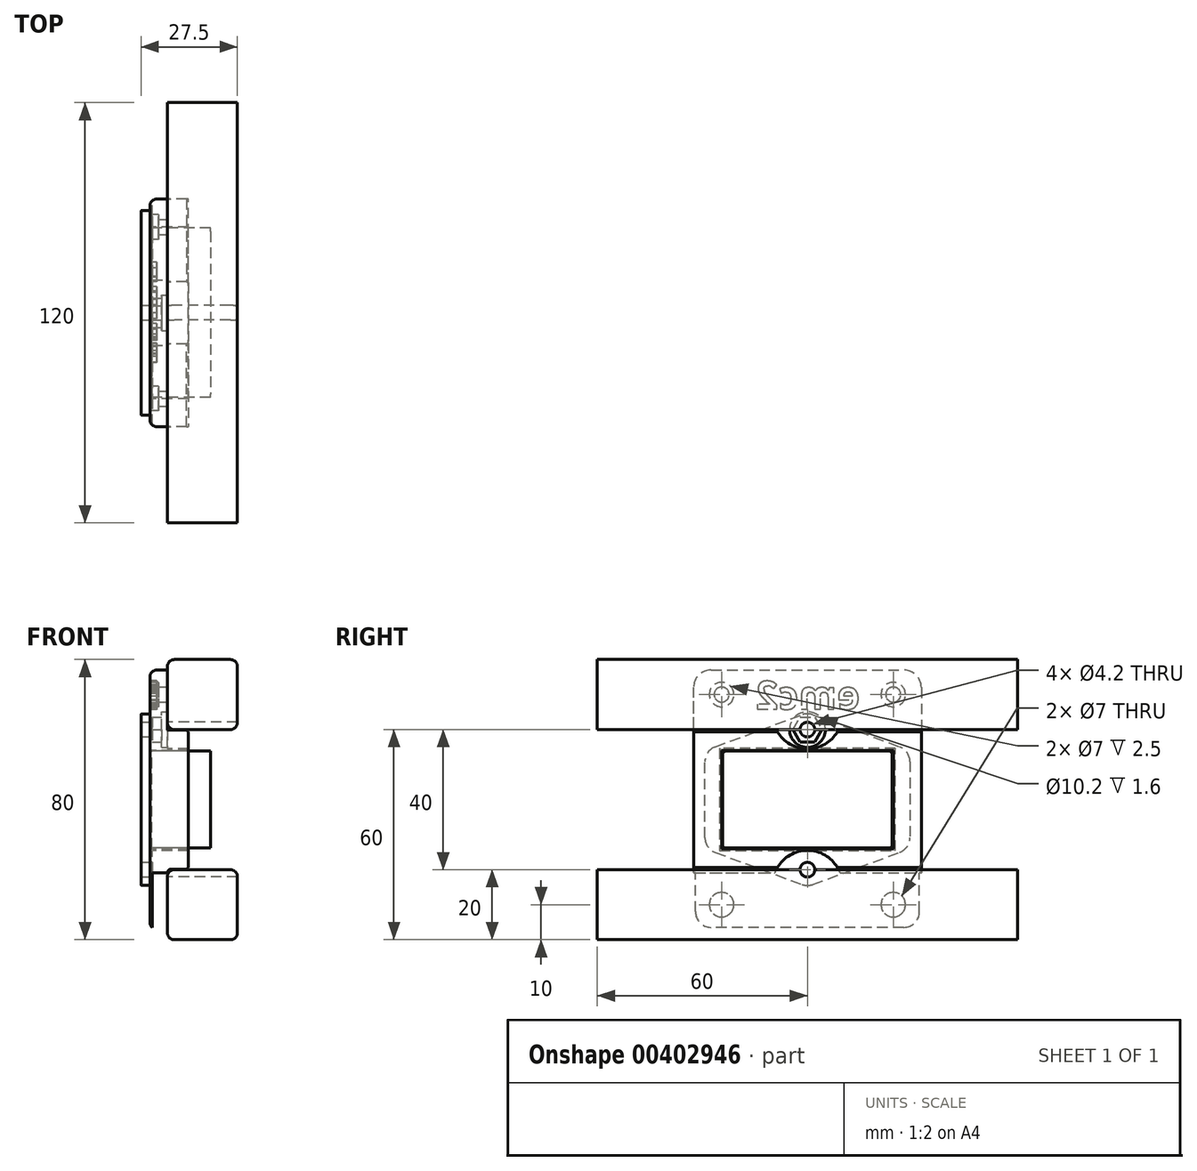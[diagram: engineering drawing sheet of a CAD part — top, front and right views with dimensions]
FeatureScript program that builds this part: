
annotation { "Feature Type Name" : "Feature", "Feature Type Description" : "" }
export const myFeature = defineFeature(function(context is Context, id is Id, definition is map)
    precondition{}
    {
        {
            var Q0;
            Q0=qCreatedBy(makeId("Right.planeOp"),FACE);
            var sketch = newSketch(context, id + "F0", { "sketchPlane" : qUnion([Q0])});
            skLineSegment(sketch, "E0.bottom", {"start": v(-32.5, 19.9) * mm, "end": v(32.5, 19.9) * mm});
            skLineSegment(sketch, "E0.top", {"start": v(-32.5, -19.9) * mm, "end": v(32.5, -19.9) * mm});
            skLineSegment(sketch, "E0.left", {"start": v(-32.5, 19.9) * mm, "end": v(-32.5, -19.9) * mm});
            skLineSegment(sketch, "E0.right", {"start": v(32.5, 19.9) * mm, "end": v(32.5, -19.9) * mm});
            skLineSegment(sketch, "E1.bottom", {"start": v(-24.5, 14) * mm, "end": v(24.5, 14) * mm});
            skLineSegment(sketch, "E1.top", {"start": v(-24.5, -14) * mm, "end": v(24.5, -14) * mm});
            skLineSegment(sketch, "E1.left", {"start": v(-24.5, 14) * mm, "end": v(-24.5, -14) * mm});
            skLineSegment(sketch, "E1.right", {"start": v(24.5, 14) * mm, "end": v(24.5, -14) * mm});
            skLineSegment(sketch, "E2", {"start": v(-32.5, 19.9) * mm, "end": v(-32.5, 37) * mm});
            skLineSegment(sketch, "E3", {"start": v(-32.5, 37) * mm, "end": v(32.5, 37) * mm});
            skLineSegment(sketch, "E4", {"start": v(32.5, 37) * mm, "end": v(32.5, 19.9) * mm});
            skLineSegment(sketch, "E5", {"start": v(-32.5, -19.9) * mm, "end": v(-32.5, -37) * mm});
            skLineSegment(sketch, "E6", {"start": v(-32.5, -37) * mm, "end": v(32.5, -37) * mm});
            skLineSegment(sketch, "E7", {"start": v(32.5, -37) * mm, "end": v(32.5, -19.9) * mm});
            skCircle(sketch, "E8", {"center": v(24.5, 30) * mm, "radius": 2.15 * mm});
            skCircle(sketch, "E9", {"center": v(-24.5, 30) * mm, "radius": 2.15 * mm});
            skCircle(sketch, "E10.MirrorC", {"center": v(-24.5, -30) * mm, "radius": 2.15 * mm});
            skCircle(sketch, "E11.MirrorC", {"center": v(24.5, -30) * mm, "radius": 2.15 * mm});
            skArc(sketch, "E12", {"start": v(-8.88, 19.9) * mm, "mid": v(0, 14.5) * mm, "end": v(8.88, 19.9) * mm});
            skArc(sketch, "E13.MirrorCS", {"start": v(-8.88, -19.9) * mm, "mid": v(0, -14.5) * mm, "end": v(8.88, -19.9) * mm});
            skSolve(sketch);
        }
        {
            var Q0;
            {var subQ1=sQuery(id+"F0.wireOp",EDGE,"E0.left");Q0=makeQuery(id+"F0.imprint","IMPRINT",FACE,{"disambiguationData":[TD([[makeQuery(id+"F0.imprint","IMPRINT",EDGE,{"derivedFrom":subQ1}),1.0]])]});}
            extrude(context, id + "F1", {"entities" : qUnion([Q0]), "depth" : 6 * mm});
        }
        {
            var Q0;
            {var subQ0=sQuery(id+"F0.wireOp",EDGE,"E12");Q0=makeQuery(id+"F0.imprint","IMPRINT",FACE,{"disambiguationData":[TD([[makeQuery(id+"F0.imprint","IMPRINT",EDGE,{"derivedFrom":subQ0}),1.0]])]});}
            var Q1;
            Q1=makeQuery(id+"F0.imprint","IMPRINT",FACE,{"disambiguationData":[TD([[makeQuery(id+"F0.imprint","IMPRINT",EDGE,{"derivedFrom":sQuery(id+"F0.wireOp",EDGE,"E0.top")}),1.0]])]});
            var Q2;
            {var subQ5=sQuery(id+"F0.wireOp",EDGE,"E2");Q2=makeQuery(id+"F0.imprint","IMPRINT",FACE,{"disambiguationData":[TD([[makeQuery(id+"F0.imprint","IMPRINT",EDGE,{"derivedFrom":subQ5}),-1.0]])]});}
            var Q3;
            Q3=makeQuery(id+"F0.imprint","IMPRINT",FACE,{"disambiguationData":[TD([[makeQuery(id+"F0.imprint","IMPRINT",EDGE,{"derivedFrom":sQuery(id+"F0.wireOp",EDGE,"E0.top")}),-1.0]])]});
            var Q4;
            {var subQ1=sQuery(id+"F0.wireOp",EDGE,"E0.left");Q4=makeQuery(id+"F0.imprint","IMPRINT",FACE,{"disambiguationData":[TD([[makeQuery(id+"F0.imprint","IMPRINT",EDGE,{"derivedFrom":subQ1}),1.0]])]});}
            extrude(context, id + "F2", {"entities" : qUnion([Q0, Q1, Q2, Q3, Q4]), "operationType" : NewBodyOperationType.ADD, "oppositeDirection" : true, "depth" : 5 * mm});
        }
        {
            var Q0;
            Q0=qCreatedBy(makeId("Front.planeOp"),FACE);
            var sketch = newSketch(context, id + "F3", { "sketchPlane" : qUnion([Q0])});
            skLineSegment(sketch, "E14.bottom", {"start": v(2, 40) * mm, "end": v(18, 40) * mm});
            skLineSegment(sketch, "E14.top", {"start": v(2, 20) * mm, "end": v(18, 20) * mm});
            skLineSegment(sketch, "E14.left", {"start": v(0, 38) * mm, "end": v(0, 22) * mm});
            skLineSegment(sketch, "E14.right", {"start": v(20, 38) * mm, "end": v(20, 22) * mm});
            skPoint(sketch, "E15.visualSharp", {"position": v(0, 40) * mm});
            skArc(sketch, "E15.filletArc", {"start": v(2, 40) * mm, "mid": v(0.59, 39.41) * mm, "end": v(0, 38) * mm});
            skPoint(sketch, "E16.visualSharp", {"position": v(20, 40) * mm});
            skArc(sketch, "E16.filletArc", {"start": v(20, 38) * mm, "mid": v(19.41, 39.41) * mm, "end": v(18, 40) * mm});
            skPoint(sketch, "E17.visualSharp", {"position": v(20, 20) * mm});
            skArc(sketch, "E17.filletArc", {"start": v(18, 20) * mm, "mid": v(19.41, 20.59) * mm, "end": v(20, 22) * mm});
            skPoint(sketch, "E18.visualSharp", {"position": v(0, 20) * mm});
            skArc(sketch, "E18.filletArc", {"start": v(0, 22) * mm, "mid": v(0.59, 20.59) * mm, "end": v(2, 20) * mm});
            skArc(sketch, "E19.MirrorCS", {"start": v(2, -40) * mm, "mid": v(0.59, -39.41) * mm, "end": v(0, -38) * mm});
            skArc(sketch, "E20.MirrorCS", {"start": v(0, -22) * mm, "mid": v(0.59, -20.59) * mm, "end": v(2, -20) * mm});
            skArc(sketch, "E21.MirrorCS", {"start": v(18, -20) * mm, "mid": v(19.41, -20.59) * mm, "end": v(20, -22) * mm});
            skArc(sketch, "E22.MirrorCS", {"start": v(20, -38) * mm, "mid": v(19.41, -39.41) * mm, "end": v(18, -40) * mm});
            skPoint(sketch, "E23.MirrorP", {"position": v(20, -40) * mm});
            skLineSegment(sketch, "E24.MirrorCS", {"start": v(2, -40) * mm, "end": v(18, -40) * mm});
            skPoint(sketch, "E25.MirrorP", {"position": v(0, -40) * mm});
            skPoint(sketch, "E26.MirrorP", {"position": v(0, -20) * mm});
            skLineSegment(sketch, "E27.MirrorCS", {"start": v(2, -20) * mm, "end": v(18, -20) * mm});
            skPoint(sketch, "E28.MirrorP", {"position": v(20, -20) * mm});
            skLineSegment(sketch, "E29.MirrorCS", {"start": v(0, -38) * mm, "end": v(0, -22) * mm});
            skLineSegment(sketch, "E30.MirrorCS", {"start": v(20, -38) * mm, "end": v(20, -22) * mm});
            skSolve(sketch);
        }
        {
            var Q0;
            Q0 = qSketchRegion(id + "F3", true);
            extrude(context, id + "F4", {"entities" : qUnion([Q0]), "endBound" : BoundingType.SYMMETRIC, "depth" : 120 * mm});
        }
        {
            var Q0;
            Q0=makeQuery(id+"F2.opExtrude","CAP_FACE",FACE,{"disambiguationData":[OSD([sQuery(id+"F0.wireOp",EDGE,"E0.left"),sQuery(id+"F0.wireOp",EDGE,"E0.right"),sQuery(id+"F0.wireOp",EDGE,"E1.bottom"),sQuery(id+"F0.wireOp",EDGE,"E1.top"),sQuery(id+"F0.wireOp",EDGE,"E1.left"),sQuery(id+"F0.wireOp",EDGE,"E1.right"),sQuery(id+"F0.wireOp",EDGE,"E2"),sQuery(id+"F0.wireOp",EDGE,"E3"),sQuery(id+"F0.wireOp",EDGE,"E4"),sQuery(id+"F0.wireOp",EDGE,"E5"),sQuery(id+"F0.wireOp",EDGE,"E6"),sQuery(id+"F0.wireOp",EDGE,"E7"),sQuery(id+"F0.wireOp",EDGE,"E8"),sQuery(id+"F0.wireOp",EDGE,"E9"),sQuery(id+"F0.wireOp",EDGE,"E10.MirrorC"),sQuery(id+"F0.wireOp",EDGE,"E11.MirrorC")])],"isStart":false});
            var sketch = newSketch(context, id + "F5", { "sketchPlane" : qUnion([Q0])});
            skLineSegment(sketch, "E31.bottom", {"start": v(-24.2, 13.85) * mm, "end": v(24.2, 13.85) * mm});
            skLineSegment(sketch, "E31.top", {"start": v(-24.2, -13.85) * mm, "end": v(24.2, -13.85) * mm});
            skLineSegment(sketch, "E31.left", {"start": v(-24.2, 13.85) * mm, "end": v(-24.2, -13.85) * mm});
            skLineSegment(sketch, "E31.right", {"start": v(24.2, 13.85) * mm, "end": v(24.2, -13.85) * mm});
            skLineSegment(sketch, "E32", {"start": v(29.25, 0) * mm, "end": v(29.25, 10.86) * mm});
            skLineSegment(sketch, "E33", {"start": v(26.3, 15.09) * mm, "end": v(1.56, 24.22) * mm});
            skLineSegment(sketch, "E34", {"start": v(-1.56, 24.22) * mm, "end": v(-26.3, 15.09) * mm});
            skLineSegment(sketch, "E35", {"start": v(-29.25, 10.86) * mm, "end": v(-29.25, 0) * mm});
            skPoint(sketch, "E36.visualSharp", {"position": v(0, 24.8) * mm});
            skArc(sketch, "E36.filletArc", {"start": v(1.56, 24.22) * mm, "mid": v(0, 24.5) * mm, "end": v(-1.56, 24.22) * mm});
            skPoint(sketch, "E37.visualSharp", {"position": v(-29.25, 14) * mm});
            skArc(sketch, "E37.filletArc", {"start": v(-26.3, 15.09) * mm, "mid": v(-28.44, 13.44) * mm, "end": v(-29.25, 10.86) * mm});
            skPoint(sketch, "E38.visualSharp", {"position": v(29.25, 14) * mm});
            skArc(sketch, "E38.filletArc", {"start": v(29.25, 10.86) * mm, "mid": v(28.44, 13.44) * mm, "end": v(26.3, 15.09) * mm});
            skLineSegment(sketch, "E39.MirrorCS", {"start": v(-29.25, -10.86) * mm, "end": v(-29.25, 0) * mm});
            skArc(sketch, "E40.MirrorCS", {"start": v(-26.3, -15.09) * mm, "mid": v(-28.44, -13.44) * mm, "end": v(-29.25, -10.86) * mm});
            skLineSegment(sketch, "E41.MirrorCS", {"start": v(-1.56, -24.22) * mm, "end": v(-26.3, -15.09) * mm});
            skLineSegment(sketch, "E42.MirrorCS", {"start": v(26.3, -15.09) * mm, "end": v(1.56, -24.22) * mm});
            skArc(sketch, "E43.MirrorCS", {"start": v(29.25, -10.86) * mm, "mid": v(28.44, -13.44) * mm, "end": v(26.3, -15.09) * mm});
            skLineSegment(sketch, "E44.MirrorCS", {"start": v(29.25, 0) * mm, "end": v(29.25, -10.86) * mm});
            skArc(sketch, "E45.MirrorCS", {"start": v(1.56, -24.22) * mm, "mid": v(0, -24.5) * mm, "end": v(-1.56, -24.22) * mm});
            skCircle(sketch, "E46", {"center": v(0, 20) * mm, "radius": 2.1 * mm});
            skCircle(sketch, "E47.MirrorC", {"center": v(0, -20) * mm, "radius": 2.1 * mm});
            skSolve(sketch);
        }
        {
            var Q0;
            Q0 = qSketchRegion(id + "F5", true);
            var Q1;
            Q1=makeQuery(id+"F5.imprint","IMPRINT",FACE,{"disambiguationData":[TD([[makeQuery(id+"F5.imprint","IMPRINT",EDGE,{"derivedFrom":sQuery(id+"F5.wireOp",EDGE,"E31.bottom")}),-1.0]])]});
            extrude(context, id + "F6", {"entities" : qUnion([Q0, Q1]), "depth" : 2.5 * mm});
        }
        {
            var Q0;
            Q0=makeQuery(id+"F5.imprint","IMPRINT",FACE,{"disambiguationData":[TD([[makeQuery(id+"F5.imprint","IMPRINT",EDGE,{"derivedFrom":sQuery(id+"F5.wireOp",EDGE,"E31.bottom")}),-1.0]])]});
            extrude(context, id + "F7", {"entities" : qUnion([Q0]), "operationType" : NewBodyOperationType.ADD, "oppositeDirection" : true, "depth" : 17.3 * mm});
        }
        {
            var Q0;
            Q0=makeQuery(id+"F7.opExtrude","SWEPT_EDGE",EDGE,{"disambiguationData":[OSD([sQuery(id+"F5.wireOp",EDGE,"E31.bottom"),sQuery(id+"F5.wireOp",EDGE,"E31.right")])]});
            var Q1;
            Q1=makeQuery(id+"F7.opExtrude","SWEPT_EDGE",EDGE,{"disambiguationData":[OSD([sQuery(id+"F5.wireOp",EDGE,"E31.top"),sQuery(id+"F5.wireOp",EDGE,"E31.right")])]});
            var Q2;
            Q2=makeQuery(id+"F7.opExtrude","SWEPT_EDGE",EDGE,{"disambiguationData":[OSD([sQuery(id+"F5.wireOp",EDGE,"E31.top"),sQuery(id+"F5.wireOp",EDGE,"E31.left")])]});
            var Q3;
            Q3=makeQuery(id+"F7.opExtrude","SWEPT_EDGE",EDGE,{"disambiguationData":[OSD([sQuery(id+"F5.wireOp",EDGE,"E31.bottom"),sQuery(id+"F5.wireOp",EDGE,"E31.left")])]});
            fillet(context, id + "F8", {"entities" : qUnion([Q0, Q1, Q2, Q3]), "radius" : 1 * mm, "tangentPropagation" : true, "allowEdgeOverflow" : false});
        }
        {
            var Q0;
            Q0=makeQuery(id+"F6.opExtrude","CAP_EDGE",EDGE,{"disambiguationData":[OSD([sQuery(id+"F5.wireOp",EDGE,"E33")])],"isStart":false});
            fillet(context, id + "F9", {"entities" : qUnion([Q0]), "radius" : 0.2 * mm, "tangentPropagation" : true, "allowEdgeOverflow" : false});
        }
        {
            var Q0;
            Q0=makeQuery(id+"F2.opExtrude","SWEPT_EDGE",EDGE,{"disambiguationData":[OSD([sQuery(id+"F0.wireOp",EDGE,"E2"),sQuery(id+"F0.wireOp",EDGE,"E3")])]});
            var Q1;
            Q1=makeQuery(id+"F2.opExtrude","SWEPT_EDGE",EDGE,{"disambiguationData":[OSD([sQuery(id+"F0.wireOp",EDGE,"E3"),sQuery(id+"F0.wireOp",EDGE,"E4")])]});
            var Q2;
            Q2=makeQuery(id+"F2.opExtrude","SWEPT_EDGE",EDGE,{"disambiguationData":[OSD([sQuery(id+"F0.wireOp",EDGE,"E6"),sQuery(id+"F0.wireOp",EDGE,"E7")])]});
            var Q3;
            Q3=makeQuery(id+"F2.opExtrude","SWEPT_EDGE",EDGE,{"disambiguationData":[OSD([sQuery(id+"F0.wireOp",EDGE,"E5"),sQuery(id+"F0.wireOp",EDGE,"E6")])]});
            fillet(context, id + "F10", {"entities" : qUnion([Q0, Q1, Q2, Q3]), "radius" : 5 * mm, "tangentPropagation" : true, "allowEdgeOverflow" : false});
        }
        {
            var Q0;
            Q0=makeQuery(id+"F2.opExtrude","CAP_EDGE",EDGE,{"disambiguationData":[OSD([sQuery(id+"F0.wireOp",EDGE,"E3")])],"isStart":false});
            var Q1;
            Q1=makeQuery(id+"F2.opExtrude","CAP_EDGE",EDGE,{"disambiguationData":[OSD([sQuery(id+"F0.wireOp",EDGE,"E6")])],"isStart":false});
            fillet(context, id + "F11", {"entities" : qUnion([Q0, Q1]), "radius" : 2 * mm, "tangentPropagation" : true, "allowEdgeOverflow" : false});
        }
        {
            var Q0;
            Q0=makeQuery(id+"F1.opExtrude","CAP_EDGE",EDGE,{"disambiguationData":[OSD([sQuery(id+"F0.wireOp",EDGE,"E0.bottom")])],"isStart":false});
            var Q1;
            Q1=makeQuery(id+"F1.opExtrude","CAP_EDGE",EDGE,{"disambiguationData":[OSD([sQuery(id+"F0.wireOp",EDGE,"E0.top")])],"isStart":false});
            chamfer(context, id + "F12", {"entities" : qUnion([Q0, Q1]), "width" : 0.5 * mm, "tangentPropagation" : true});
        }
        {
            var Q0;
            Q0=makeQuery(id+"F1.opExtrude","CAP_EDGE",EDGE,{"disambiguationData":[OSD([sQuery(id+"F0.wireOp",EDGE,"E0.bottom")])],"isStart":true});
            var Q1;
            Q1=makeQuery(id+"F1.opExtrude","CAP_EDGE",EDGE,{"disambiguationData":[OSD([sQuery(id+"F0.wireOp",EDGE,"E0.top")])],"isStart":true});
            fillet(context, id + "F13", {"entities" : qUnion([Q0, Q1]), "radius" : 1 * mm, "tangentPropagation" : true, "allowEdgeOverflow" : false});
        }
        {
            var Q0;
            Q0=makeQuery(id+"F2.opExtrude","CAP_FACE",FACE,{"disambiguationData":[OSD([sQuery(id+"F0.wireOp",EDGE,"E0.left"),sQuery(id+"F0.wireOp",EDGE,"E0.right"),sQuery(id+"F0.wireOp",EDGE,"E1.bottom"),sQuery(id+"F0.wireOp",EDGE,"E1.top"),sQuery(id+"F0.wireOp",EDGE,"E1.left"),sQuery(id+"F0.wireOp",EDGE,"E1.right"),sQuery(id+"F0.wireOp",EDGE,"E2"),sQuery(id+"F0.wireOp",EDGE,"E3"),sQuery(id+"F0.wireOp",EDGE,"E4"),sQuery(id+"F0.wireOp",EDGE,"E5"),sQuery(id+"F0.wireOp",EDGE,"E6"),sQuery(id+"F0.wireOp",EDGE,"E7"),sQuery(id+"F0.wireOp",EDGE,"E8"),sQuery(id+"F0.wireOp",EDGE,"E9"),sQuery(id+"F0.wireOp",EDGE,"E10.MirrorC"),sQuery(id+"F0.wireOp",EDGE,"E11.MirrorC")])],"isStart":false});
            var sketch = newSketch(context, id + "F14", { "sketchPlane" : qUnion([Q0])});
            skCircle(sketch, "E48.0", {"center": v(0, 20) * mm, "radius": 2.1 * mm});
            skCircle(sketch, "E49.0", {"center": v(0, -20) * mm, "radius": 2.1 * mm});
            skSolve(sketch);
        }
        {
            var Q0;
            Q0 = qSketchRegion(id + "F14", true);
            extrude(context, id + "F15", {"entities" : qUnion([Q0]), "operationType" : NewBodyOperationType.REMOVE, "oppositeDirection" : true, "depth" : 25 * mm});
        }
        {
            var Q0;
            {var subQ0=sQuery(id+"F0.wireOp",EDGE,"E0.right");var subQ1=sQuery(id+"F0.wireOp",EDGE,"E7");var subQ2=sQuery(id+"F0.wireOp",EDGE,"E4");var subQ3=sQuery(id+"F0.wireOp",EDGE,"E0.left");var subQ4=sQuery(id+"F0.wireOp",EDGE,"E5");var subQ5=sQuery(id+"F0.wireOp",EDGE,"E2");var subQ7=sQuery(id+"F0.wireOp",EDGE,"E12");var subQ8=sQuery(id+"F0.wireOp",EDGE,"E9");var subQ9=sQuery(id+"F0.wireOp",EDGE,"E3");var subQ10=sQuery(id+"F0.wireOp",EDGE,"E8");Q0=makeQuery(id+"F2.boolean.opBoolean","SPLIT",FACE,{"disambiguationData":[TD([makeQuery(id+"F1.opExtrude","SWEPT_FACE",FACE,{"disambiguationData":[OSD([subQ7])]})])],"derivedFrom":makeQuery(id+"F2.opExtrude","CAP_FACE",FACE,{"disambiguationData":[OSD([subQ3,subQ0,subQ5,subQ9,subQ2,subQ4,sQuery(id+"F0.wireOp",EDGE,"E6"),subQ1,subQ10,subQ8,sQuery(id+"F0.wireOp",EDGE,"E10.MirrorC"),sQuery(id+"F0.wireOp",EDGE,"E11.MirrorC")])],"isStart":true})});}
            var sketch = newSketch(context, id + "F16", { "sketchPlane" : qUnion([Q0])});
            skCircle(sketch, "E50", {"center": v(0, 20) * mm, "radius": 5.1 * mm});
            skCircle(sketch, "E51.cCircle", {"center": v(0, 20) * mm, "radius": 3.6 * mm, "construction": true});
            skLineSegment(sketch, "E51.0", {"start": v(2.08, 16.4) * mm, "end": v(-2.08, 16.4) * mm});
            skLineSegment(sketch, "E51.1", {"start": v(-2.08, 16.4) * mm, "end": v(-4.16, 20) * mm});
            skLineSegment(sketch, "E51.2", {"start": v(-4.16, 20) * mm, "end": v(-2.08, 23.6) * mm});
            skLineSegment(sketch, "E51.3", {"start": v(-2.08, 23.6) * mm, "end": v(2.08, 23.6) * mm});
            skLineSegment(sketch, "E51.4", {"start": v(2.08, 23.6) * mm, "end": v(4.16, 20) * mm});
            skLineSegment(sketch, "E51.5", {"start": v(4.16, 20) * mm, "end": v(2.08, 16.4) * mm});
            skPoint(sketch, "E51.0.midPoint", {"position": v(0, 16.4) * mm});
            skCircle(sketch, "E52.MirrorC", {"center": v(0, -20) * mm, "radius": 5.1 * mm});
            skCircle(sketch, "E53.MirrorC", {"center": v(0, -20) * mm, "radius": 3.6 * mm, "construction": true});
            skLineSegment(sketch, "E54.MirrorCS", {"start": v(-2.08, -16.4) * mm, "end": v(-4.16, -20) * mm});
            skLineSegment(sketch, "E55.MirrorCS", {"start": v(-2.08, -23.6) * mm, "end": v(2.08, -23.6) * mm});
            skLineSegment(sketch, "E56.MirrorCS", {"start": v(2.08, -23.6) * mm, "end": v(4.16, -20) * mm});
            skLineSegment(sketch, "E57.MirrorCS", {"start": v(4.16, -20) * mm, "end": v(2.08, -16.4) * mm});
            skLineSegment(sketch, "E58.MirrorCS", {"start": v(2.08, -16.4) * mm, "end": v(-2.08, -16.4) * mm});
            skLineSegment(sketch, "E59", {"start": v(-2.08, -23.6) * mm, "end": v(-4.16, -20) * mm});
            skSolve(sketch);
        }
        {
            var Q0;
            Q0=makeQuery(id+"F16.imprint","IMPRINT",FACE,{"disambiguationData":[TD([[makeQuery(id+"F16.imprint","IMPRINT",EDGE,{"derivedFrom":sQuery(id+"F16.wireOp",EDGE,"E50")}),1.0]])]});
            var Q1;
            Q1=makeQuery(id+"F16.imprint","IMPRINT",FACE,{"disambiguationData":[TD([[makeQuery(id+"F16.imprint","IMPRINT",EDGE,{"derivedFrom":sQuery(id+"F16.wireOp",EDGE,"E52.MirrorC")}),-1.0]])]});
            extrude(context, id + "F17", {"entities" : qUnion([Q0, Q1]), "operationType" : NewBodyOperationType.REMOVE, "oppositeDirection" : true, "depth" : 1.6 * mm});
        }
        {
            var Q0;
            {var subQ0=sQuery(id+"F0.wireOp",EDGE,"E0.right");var subQ1=sQuery(id+"F0.wireOp",EDGE,"E7");var subQ2=sQuery(id+"F0.wireOp",EDGE,"E4");var subQ3=sQuery(id+"F0.wireOp",EDGE,"E0.left");var subQ4=sQuery(id+"F0.wireOp",EDGE,"E5");var subQ5=sQuery(id+"F0.wireOp",EDGE,"E2");var subQ7=sQuery(id+"F0.wireOp",EDGE,"E12");var subQ8=sQuery(id+"F0.wireOp",EDGE,"E9");var subQ9=sQuery(id+"F0.wireOp",EDGE,"E3");var subQ10=sQuery(id+"F0.wireOp",EDGE,"E8");Q0=makeQuery(id+"F17.boolean.opBoolean","SPLIT",FACE,{"disambiguationData":[TD([makeQuery(id+"F15.boolean.opBoolean","COPY",FACE,{"derivedFrom":makeQuery(id+"F15.opExtrude","SWEPT_FACE",FACE,{"disambiguationData":[OSD([sQuery(id+"F14.wireOp",EDGE,"E48.0")])]})})])],"derivedFrom":makeQuery(id+"F2.boolean.opBoolean","SPLIT",FACE,{"disambiguationData":[TD([makeQuery(id+"F1.opExtrude","SWEPT_FACE",FACE,{"disambiguationData":[OSD([subQ7])]})])],"derivedFrom":makeQuery(id+"F2.opExtrude","CAP_FACE",FACE,{"disambiguationData":[OSD([subQ3,subQ0,subQ5,subQ9,subQ2,subQ4,sQuery(id+"F0.wireOp",EDGE,"E6"),subQ1,subQ10,subQ8,sQuery(id+"F0.wireOp",EDGE,"E10.MirrorC"),sQuery(id+"F0.wireOp",EDGE,"E11.MirrorC")])],"isStart":true})})});}
            var Q1;
            {var subQ0=sQuery(id+"F0.wireOp",EDGE,"E0.right");var subQ1=sQuery(id+"F0.wireOp",EDGE,"E7");var subQ2=sQuery(id+"F0.wireOp",EDGE,"E4");var subQ3=sQuery(id+"F0.wireOp",EDGE,"E0.left");var subQ4=sQuery(id+"F0.wireOp",EDGE,"E5");var subQ5=sQuery(id+"F0.wireOp",EDGE,"E2");var subQ7=sQuery(id+"F0.wireOp",EDGE,"E13.MirrorCS");var subQ8=sQuery(id+"F0.wireOp",EDGE,"E11.MirrorC");var subQ9=sQuery(id+"F0.wireOp",EDGE,"E6");var subQ10=sQuery(id+"F0.wireOp",EDGE,"E10.MirrorC");Q1=makeQuery(id+"F17.boolean.opBoolean","SPLIT",FACE,{"disambiguationData":[TD([makeQuery(id+"F15.boolean.opBoolean","COPY",FACE,{"derivedFrom":makeQuery(id+"F15.opExtrude","SWEPT_FACE",FACE,{"disambiguationData":[OSD([sQuery(id+"F14.wireOp",EDGE,"E49.0")])]})})])],"derivedFrom":makeQuery(id+"F2.boolean.opBoolean","SPLIT",FACE,{"disambiguationData":[TD([makeQuery(id+"F1.opExtrude","SWEPT_FACE",FACE,{"disambiguationData":[OSD([subQ7])]})])],"derivedFrom":makeQuery(id+"F2.opExtrude","CAP_FACE",FACE,{"disambiguationData":[OSD([subQ3,subQ0,subQ5,sQuery(id+"F0.wireOp",EDGE,"E3"),subQ2,subQ4,subQ9,subQ1,sQuery(id+"F0.wireOp",EDGE,"E8"),sQuery(id+"F0.wireOp",EDGE,"E9"),subQ10,subQ8])],"isStart":true})})});}
            extrude(context, id + "F18", {"entities" : qUnion([Q0, Q1]), "operationType" : NewBodyOperationType.REMOVE, "oppositeDirection" : true, "depth" : 4.35 * mm});
        }
        {
            var Q0;
            Q0=makeQuery(id+"F2.opExtrude","CAP_EDGE",EDGE,{"disambiguationData":[OSD([sQuery(id+"F0.wireOp",EDGE,"E1.bottom")])],"isStart":false});
            var Q1;
            Q1=makeQuery(id+"F2.opExtrude","CAP_EDGE",EDGE,{"disambiguationData":[OSD([sQuery(id+"F0.wireOp",EDGE,"E1.right")])],"isStart":false});
            var Q2;
            Q2=makeQuery(id+"F2.opExtrude","CAP_EDGE",EDGE,{"disambiguationData":[OSD([sQuery(id+"F0.wireOp",EDGE,"E1.top")])],"isStart":false});
            var Q3;
            Q3=makeQuery(id+"F2.opExtrude","CAP_EDGE",EDGE,{"disambiguationData":[OSD([sQuery(id+"F0.wireOp",EDGE,"E1.left")])],"isStart":false});
            chamfer(context, id + "F19", {"entities" : qUnion([Q0, Q1, Q2, Q3]), "width" : 0.6 * mm, "tangentPropagation" : true});
        }
        {
            var Q0;
            Q0=makeQuery(id+"F2.opExtrude","CAP_FACE",FACE,{"disambiguationData":[OSD([sQuery(id+"F0.wireOp",EDGE,"E0.left"),sQuery(id+"F0.wireOp",EDGE,"E0.right"),sQuery(id+"F0.wireOp",EDGE,"E1.bottom"),sQuery(id+"F0.wireOp",EDGE,"E1.top"),sQuery(id+"F0.wireOp",EDGE,"E1.left"),sQuery(id+"F0.wireOp",EDGE,"E1.right"),sQuery(id+"F0.wireOp",EDGE,"E2"),sQuery(id+"F0.wireOp",EDGE,"E3"),sQuery(id+"F0.wireOp",EDGE,"E4"),sQuery(id+"F0.wireOp",EDGE,"E5"),sQuery(id+"F0.wireOp",EDGE,"E6"),sQuery(id+"F0.wireOp",EDGE,"E7"),sQuery(id+"F0.wireOp",EDGE,"E8"),sQuery(id+"F0.wireOp",EDGE,"E9"),sQuery(id+"F0.wireOp",EDGE,"E10.MirrorC"),sQuery(id+"F0.wireOp",EDGE,"E11.MirrorC")])],"isStart":false});
            var sketch = newSketch(context, id + "F20", { "sketchPlane" : qUnion([Q0])});
            skCircle(sketch, "E60", {"center": v(24.5, 30) * mm, "radius": 3.5 * mm});
            skCircle(sketch, "E61", {"center": v(-24.5, 30) * mm, "radius": 3.5 * mm});
            skCircle(sketch, "E62", {"center": v(-24.5, -30) * mm, "radius": 3.5 * mm});
            skCircle(sketch, "E63", {"center": v(24.5, -30) * mm, "radius": 3.5 * mm});
            skSolve(sketch);
        }
        {
            var Q0;
            Q0 = qSketchRegion(id + "F20", true);
            extrude(context, id + "F21", {"entities" : qUnion([Q0]), "operationType" : NewBodyOperationType.REMOVE, "oppositeDirection" : true, "depth" : 2.5 * mm});
        }
        {
            var Q0;
            Q0=makeQuery(id+"F2.opExtrude","CAP_FACE",FACE,{"disambiguationData":[OSD([sQuery(id+"F0.wireOp",EDGE,"E0.left"),sQuery(id+"F0.wireOp",EDGE,"E0.right"),sQuery(id+"F0.wireOp",EDGE,"E1.bottom"),sQuery(id+"F0.wireOp",EDGE,"E1.top"),sQuery(id+"F0.wireOp",EDGE,"E1.left"),sQuery(id+"F0.wireOp",EDGE,"E1.right"),sQuery(id+"F0.wireOp",EDGE,"E2"),sQuery(id+"F0.wireOp",EDGE,"E3"),sQuery(id+"F0.wireOp",EDGE,"E4"),sQuery(id+"F0.wireOp",EDGE,"E5"),sQuery(id+"F0.wireOp",EDGE,"E6"),sQuery(id+"F0.wireOp",EDGE,"E7"),sQuery(id+"F0.wireOp",EDGE,"E8"),sQuery(id+"F0.wireOp",EDGE,"E9"),sQuery(id+"F0.wireOp",EDGE,"E10.MirrorC"),sQuery(id+"F0.wireOp",EDGE,"E11.MirrorC")])],"isStart":false});
            var sketch = newSketch(context, id + "F22", { "sketchPlane" : qUnion([Q0])});
            skText(sketch, "E64", { "text": "emc2\n", "fontName": "OpenSans-Bold.ttf"});
            const initialGuessF22  = {"E64": [-0.015, 0.02583, 1, 0, 0.00803]};
            skSetInitialGuess(sketch, initialGuessF22);
            skSolve(sketch);
        }
        {
            var Q0;
            Q0 = qSketchRegion(id + "F22", true);
            extrude(context, id + "F23", {"entities" : qUnion([Q0]), "operationType" : NewBodyOperationType.REMOVE, "oppositeDirection" : true, "depth" : 2 * mm});
        }
    });
